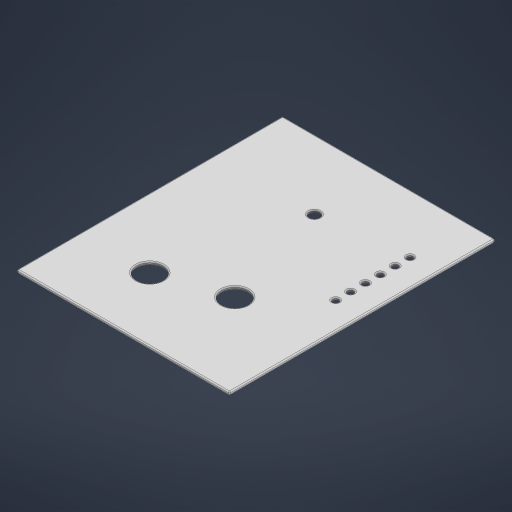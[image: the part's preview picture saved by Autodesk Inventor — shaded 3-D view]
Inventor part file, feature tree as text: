
AUTODESK INVENTOR PART (.ipt)
format: ipt  version: 2023 (Build 270158000, 158)  size: 267,776 bytes
history: native  units: mm
features: extrude x1, fillet x1, other x1
ambient origin geometry x8: Origin, YZ Plane, XZ Plane, XY Plane, X Axis, Y Axis, Z Axis, Center Point
bodies: Solid1 (feature_tree)
feature tree (3):
  extrude  "xor"  Depth=200.0mm
  fillet  "Fillet1"  Radius=250.0mm
  other  "page_lines"
